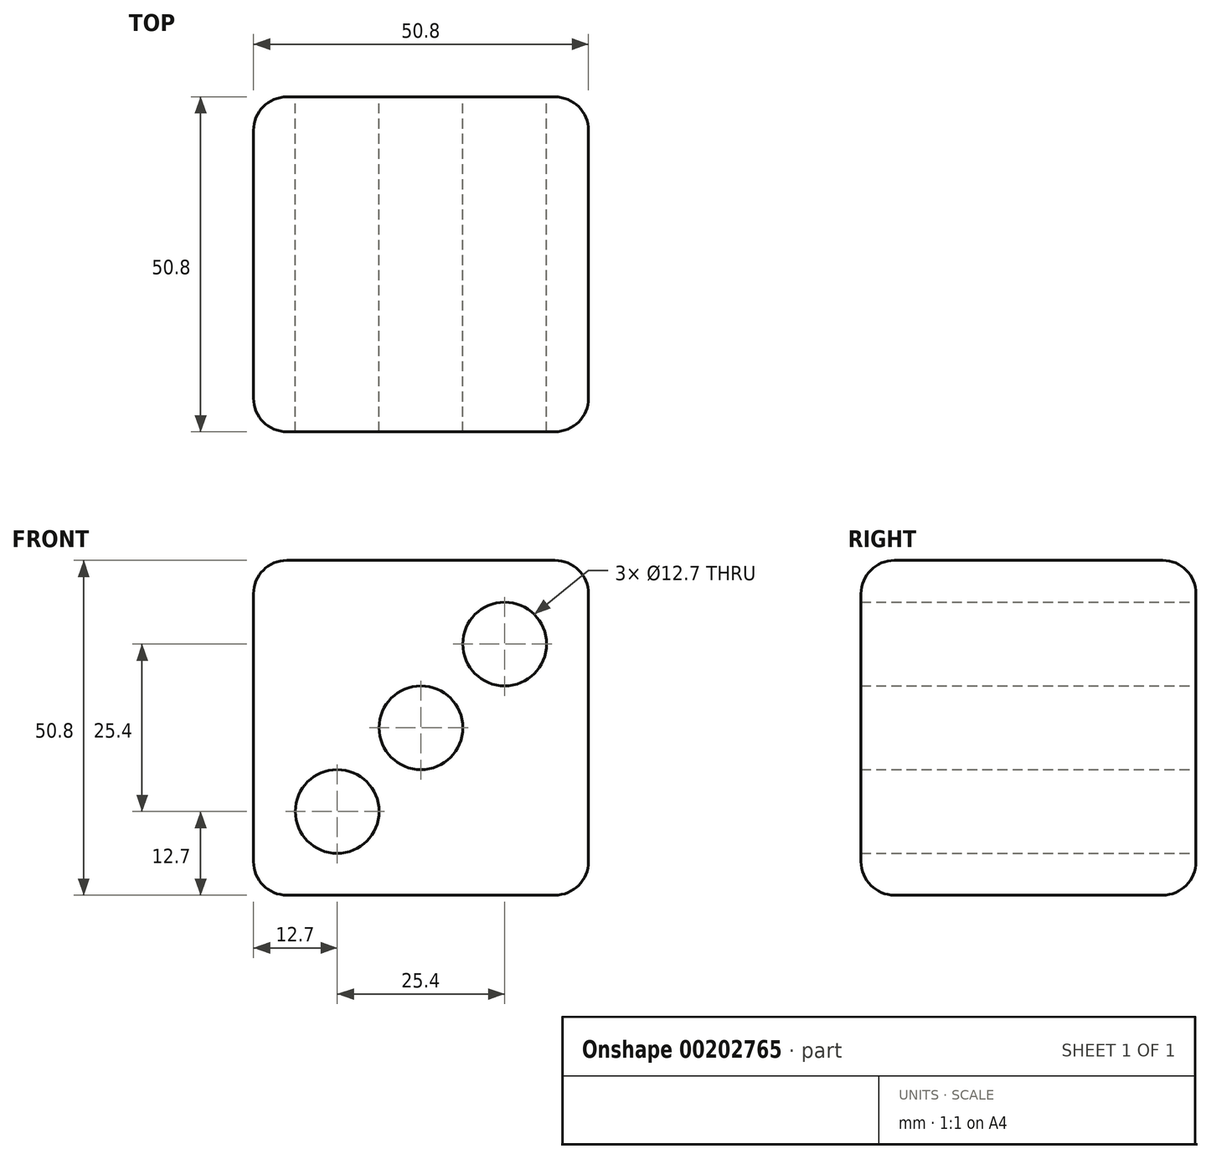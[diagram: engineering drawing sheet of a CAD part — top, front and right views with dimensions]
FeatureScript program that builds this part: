
annotation { "Feature Type Name" : "Feature", "Feature Type Description" : "" }
export const myFeature = defineFeature(function(context is Context, id is Id, definition is map)
    precondition{}
    {
        {
            var Q0;
            Q0=qCreatedBy(makeId("Front.planeOp"),FACE);
            var sketch = newSketch(context, id + "F0", { "sketchPlane" : qUnion([Q0])});
            skLineSegment(sketch, "E0.bottom", {"start": v(-25.4, 25.4) * mm, "end": v(25.4, 25.4) * mm});
            skLineSegment(sketch, "E0.top", {"start": v(-25.4, -25.4) * mm, "end": v(25.4, -25.4) * mm});
            skLineSegment(sketch, "E0.left", {"start": v(-25.4, 25.4) * mm, "end": v(-25.4, -25.4) * mm});
            skLineSegment(sketch, "E0.right", {"start": v(25.4, 25.4) * mm, "end": v(25.4, -25.4) * mm});
            skPoint(sketch, "E0.middle", {"position": v(0, 0) * mm});
            skSolve(sketch);
        }
        {
            var Q0;
            Q0 = qSketchRegion(id + "F0", true);
            var Q1;
            Q1=makeQuery(id+"F0.imprint","IMPRINT",FACE,{"disambiguationData":[TD([[makeQuery(id+"F0.imprint","IMPRINT",EDGE,{"derivedFrom":sQuery(id+"F0.wireOp",EDGE,"E0.bottom")}),-1.0]])]});
            extrude(context, id + "F1", {"entities" : qUnion([Q0, Q1]), "depth" : 50.8 * mm});
        }
        {
            var Q0;
            Q0=makeQuery(id+"F1.opExtrude","CAP_FACE",FACE,{"disambiguationData":[OSD([sQuery(id+"F0.wireOp",EDGE,"E0.bottom"),sQuery(id+"F0.wireOp",EDGE,"E0.top"),sQuery(id+"F0.wireOp",EDGE,"E0.left"),sQuery(id+"F0.wireOp",EDGE,"E0.right")])],"isStart":true});
            var sketch = newSketch(context, id + "F2", { "sketchPlane" : qUnion([Q0])});
            skLineSegment(sketch, "E1", {"start": v(0, -25.4) * mm, "end": v(0, 25.4) * mm, "construction": true});
            skCircle(sketch, "E2", {"center": v(0, 0) * mm, "radius": 6.35 * mm});
            skLineSegment(sketch, "E3", {"start": v(0, 0) * mm, "end": v(25.4, 0) * mm, "construction": true});
            skLineSegment(sketch, "E4", {"start": v(0, 0) * mm, "end": v(-25.4, 0) * mm, "construction": true});
            skLineSegment(sketch, "E5", {"start": v(0, 0) * mm, "end": v(25.4, -25.4) * mm, "construction": true});
            skCircle(sketch, "E6", {"center": v(12.7, -12.7) * mm, "radius": 6.35 * mm});
            skLineSegment(sketch, "E7", {"start": v(0, 0) * mm, "end": v(-25.4, 25.4) * mm, "construction": true});
            skCircle(sketch, "E8", {"center": v(-12.7, 12.7) * mm, "radius": 6.35 * mm});
            skSolve(sketch);
        }
        {
            var Q0;
            Q0 = qSketchRegion(id + "F2", true);
            extrude(context, id + "F3", {"entities" : qUnion([Q0]), "operationType" : NewBodyOperationType.REMOVE, "endBound" : BoundingType.THROUGH_ALL, "oppositeDirection" : true, "depth" : 25.4 * mm});
        }
        {
            var Q0;
            Q0=makeQuery(id+"F1.opExtrude","SWEPT_EDGE",EDGE,{"disambiguationData":[OSD([sQuery(id+"F0.wireOp",EDGE,"E0.bottom"),sQuery(id+"F0.wireOp",EDGE,"E0.left")])]});
            fillet(context, id + "F4", {"entities" : qUnion([Q0]), "radius" : 5.08 * mm, "tangentPropagation" : true, "allowEdgeOverflow" : false});
        }
        {
            var Q0;
            Q0=makeQuery(id+"F1.opExtrude","CAP_EDGE",EDGE,{"disambiguationData":[OSD([sQuery(id+"F0.wireOp",EDGE,"E0.left")])],"isStart":true});
            fillet(context, id + "F5", {"entities" : qUnion([Q0]), "radius" : 5.08 * mm, "tangentPropagation" : true, "allowEdgeOverflow" : false});
        }
        {
            var Q0;
            Q0=makeQuery(id+"F1.opExtrude","CAP_EDGE",EDGE,{"disambiguationData":[OSD([sQuery(id+"F0.wireOp",EDGE,"E0.left")])],"isStart":false});
            fillet(context, id + "F6", {"entities" : qUnion([Q0]), "radius" : 5.08 * mm, "tangentPropagation" : true, "allowEdgeOverflow" : false});
        }
        {
            var Q0;
            Q0=makeQuery(id+"F1.opExtrude","SWEPT_EDGE",EDGE,{"disambiguationData":[OSD([sQuery(id+"F0.wireOp",EDGE,"E0.top"),sQuery(id+"F0.wireOp",EDGE,"E0.left")])]});
            fillet(context, id + "F7", {"entities" : qUnion([Q0]), "radius" : 5.08 * mm, "tangentPropagation" : true, "allowEdgeOverflow" : false});
        }
        {
            var Q0;
            Q0=makeQuery(id+"F1.opExtrude","CAP_EDGE",EDGE,{"disambiguationData":[OSD([sQuery(id+"F0.wireOp",EDGE,"E0.right")])],"isStart":true});
            fillet(context, id + "F8", {"entities" : qUnion([Q0]), "radius" : 5.08 * mm, "tangentPropagation" : true, "allowEdgeOverflow" : false});
        }
    });
